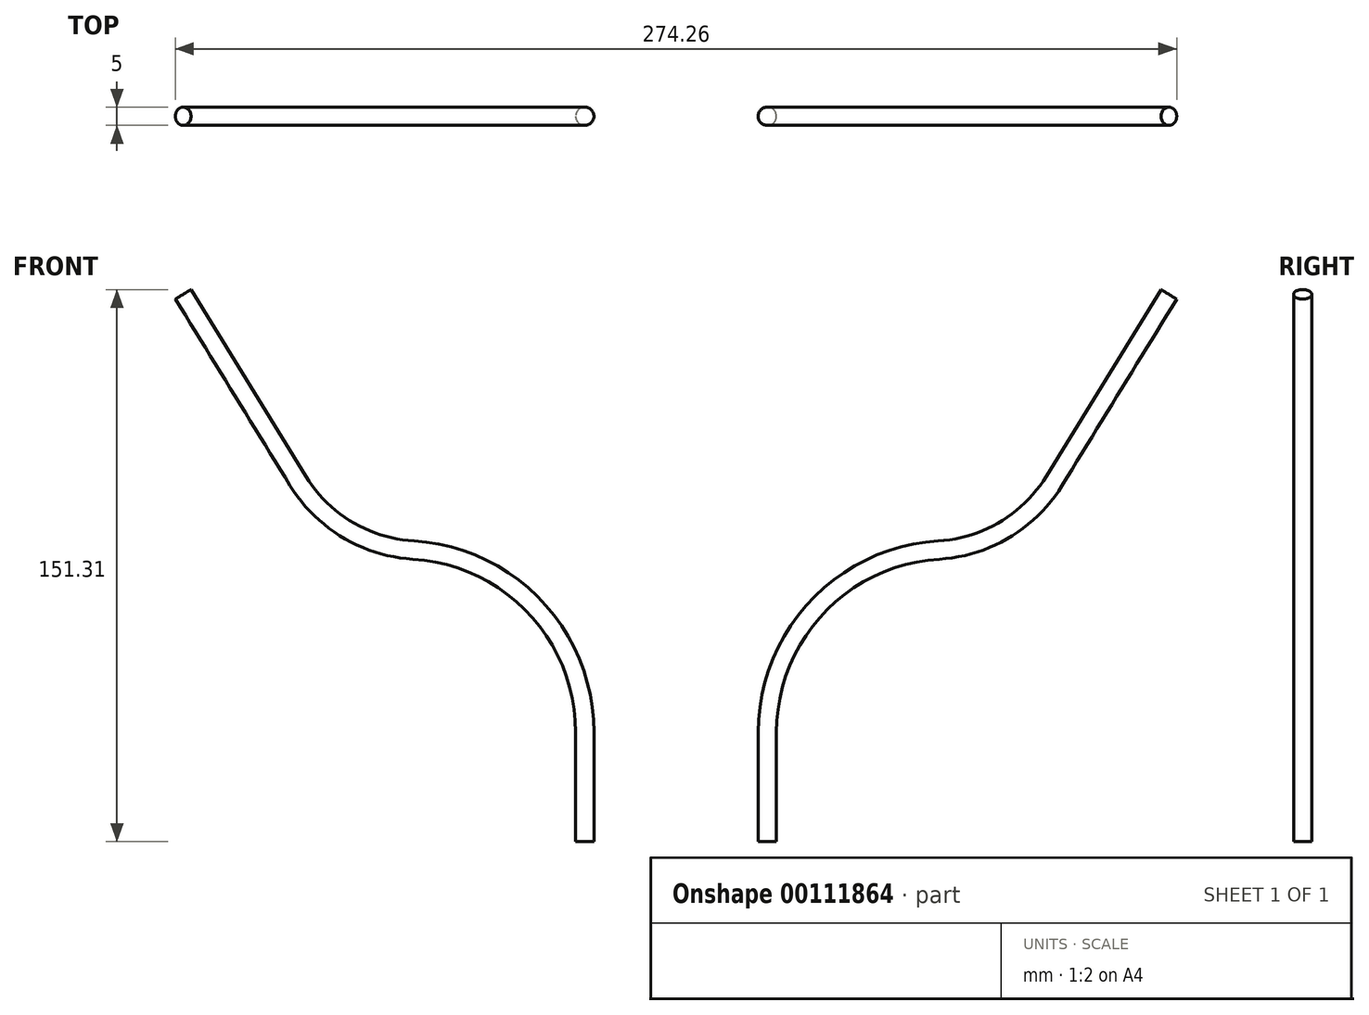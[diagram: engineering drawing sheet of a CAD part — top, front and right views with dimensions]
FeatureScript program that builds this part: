
annotation { "Feature Type Name" : "Feature", "Feature Type Description" : "" }
export const myFeature = defineFeature(function(context is Context, id is Id, definition is map)
    precondition{}
    {
        {
            var Q0;
            Q0=qCreatedBy(makeId("Top.planeOp"),FACE);
            var sketch = newSketch(context, id + "F0", { "sketchPlane" : qUnion([Q0])});
            skCircle(sketch, "E0", {"center": v(0, 0) * mm, "radius": 2.5 * mm});
            skSolve(sketch);
        }
        {
            var Q0;
            Q0=qCreatedBy(makeId("Front.planeOp"),FACE);
            var sketch = newSketch(context, id + "F1", { "sketchPlane" : qUnion([Q0])});
            skLineSegment(sketch, "E1", {"start": v(0, 0) * mm, "end": v(0, 30) * mm});
            skArc(sketch, "E2", {"start": v(46.95, 79.9) * mm, "mid": v(13.58, 64.26) * mm, "end": v(0, 30) * mm});
            skArc(sketch, "E3", {"start": v(46.95, 79.9) * mm, "mid": v(65.08, 85.53) * mm, "end": v(78.58, 98.88) * mm});
            skLineSegment(sketch, "E4", {"start": v(78.58, 98.88) * mm, "end": v(110, 150) * mm});
            skSolve(sketch);
        }
        {
            var Q0;
            Q0=makeQuery(id+"F0.imprint","IMPRINT",FACE,{"disambiguationData":[TD([[makeQuery(id+"F0.imprint","IMPRINT",EDGE,{"derivedFrom":sQuery(id+"F0.wireOp",EDGE,"E0")}),1.0]])]});
            var Q1;
            Q1=sQuery(id+"F1.wireOp",EDGE,"E1");
            var Q2;
            Q2=sQuery(id+"F1.wireOp",EDGE,"E2");
            var Q3;
            Q3=sQuery(id+"F1.wireOp",EDGE,"E3");
            var Q4;
            Q4=sQuery(id+"F1.wireOp",EDGE,"E4");
            sweep(context, id + "F2", {"profiles" : qUnion([Q0]), "path" : qUnion([Q1, Q2, Q3, Q4])});
        }
        {
            var Q0;
            Q0=qCreatedBy(makeId("Right.planeOp"),FACE);
            cPlane(context, id + "F3", {"entities" : qUnion([Q0]), "cplaneType" : CPlaneType.OFFSET, "offset" : 25 * mm, "oppositeDirection" : true, "width" : 150 * mm, "height" : 150 * mm});
        }
        {
            var Q0;
            Q0=makeQuery(id+"F2.opSweep","SWEPT_BODY",BODY,{"disambiguationData":[OSD([sQuery(id+"F0.wireOp",EDGE,"E0"),sQuery(id+"F1.wireOp",EDGE,"E4")])]});
            var Q1;
            Q1=qCreatedBy(id+"F3.planeOp",FACE);
            mirror(context, id + "F4", {"entities" : qUnion([Q0]), "mirrorPlane" : qUnion([Q1])});
        }
    });
